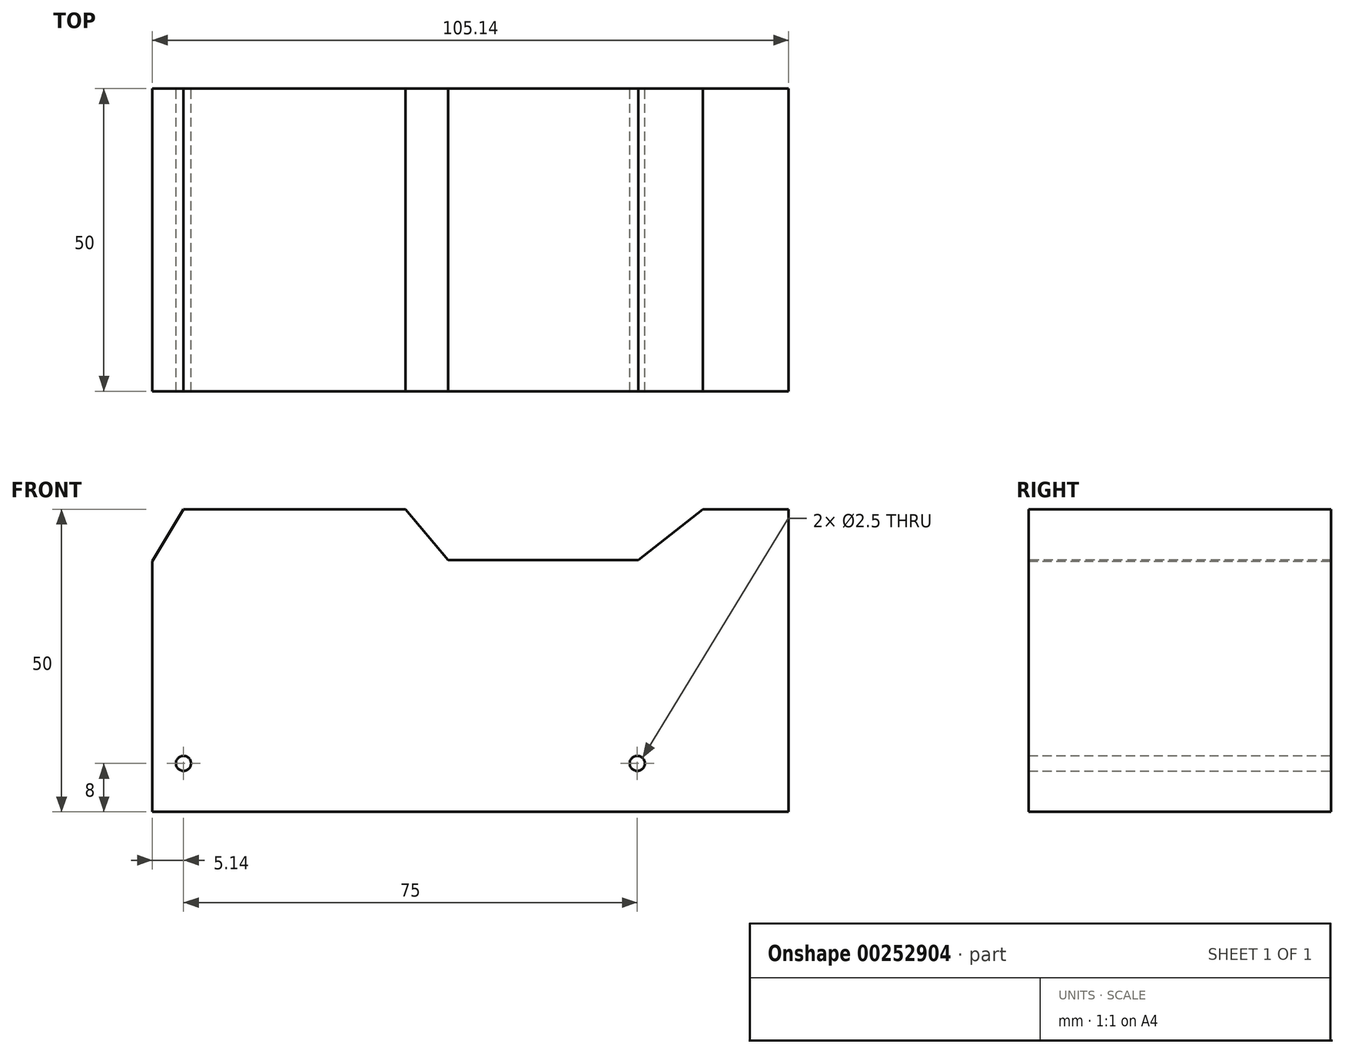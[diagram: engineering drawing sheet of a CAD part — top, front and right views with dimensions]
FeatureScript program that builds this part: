
annotation { "Feature Type Name" : "Feature", "Feature Type Description" : "" }
export const myFeature = defineFeature(function(context is Context, id is Id, definition is map)
    precondition{}
    {
        {
            var Q0;
            Q0=qCreatedBy(makeId("Front.planeOp"),FACE);
            var sketch = newSketch(context, id + "F0", { "sketchPlane" : qUnion([Q0])});
            skLineSegment(sketch, "E0.bottom", {"start": v(50, 25) * mm, "end": v(-50, 25) * mm});
            skLineSegment(sketch, "E0.top", {"start": v(50, -25) * mm, "end": v(-50, -25) * mm});
            skLineSegment(sketch, "E0.left", {"start": v(50, 25) * mm, "end": v(50, -25) * mm});
            skPoint(sketch, "E0.middle", {"position": v(0, 0) * mm});
            skLineSegment(sketch, "E1", {"start": v(-55.14, 16.43) * mm, "end": v(-50, 25) * mm});
            skLineSegment(sketch, "E2", {"start": v(50, -25) * mm, "end": v(25, -25) * mm});
            skLineSegment(sketch, "E3", {"start": v(25, -25) * mm, "end": v(25, -17) * mm});
            skLineSegment(sketch, "E4", {"start": v(-50, -18.25) * mm, "end": v(-50, -17) * mm});
            skCircle(sketch, "E5", {"center": v(-50, -17) * mm, "radius": 1.25 * mm});
            skCircle(sketch, "E6", {"center": v(25, -17) * mm, "radius": 1.25 * mm});
            skLineSegment(sketch, "E7", {"start": v(-55.14, -25) * mm, "end": v(-55.14, 16.43) * mm});
            skPoint(sketch, "E8.orphan", {"position": v(-80, -25) * mm});
            skLineSegment(sketch, "E9", {"start": v(-55.14, -25) * mm, "end": v(-50, -25) * mm});
            skSolve(sketch);
        }
        {
            var Q0;
            Q0=makeQuery(id+"F0.imprint","IMPRINT",FACE,{"disambiguationData":[TD([[makeQuery(id+"F0.imprint","IMPRINT",EDGE,{"derivedFrom":sQuery(id+"F0.wireOp",EDGE,"E0.bottom")}),1.0]])]});
            extrude(context, id + "F1", {"entities" : qUnion([Q0]), "depth" : 50 * mm});
        }
        {
            var Q0;
            Q0=makeQuery(id+"F1.opExtrude","CAP_FACE",FACE,{"disambiguationData":[OSD([sQuery(id+"F0.wireOp",EDGE,"E0.bottom"),sQuery(id+"F0.wireOp",EDGE,"E0.top"),sQuery(id+"F0.wireOp",EDGE,"E0.left"),sQuery(id+"F0.wireOp",EDGE,"AwUMNLbW-5q2J-AW1u-s40T-xbT19hCx7R6J"),sQuery(id+"F0.wireOp",EDGE,"E1"),sQuery(id+"F0.wireOp",EDGE,"E2"),sQuery(id+"F0.wireOp",EDGE,"E5"),sQuery(id+"F0.wireOp",EDGE,"E6")])],"isStart":false});
            var sketch = newSketch(context, id + "F2", { "sketchPlane" : qUnion([Q0])});
            skLineSegment(sketch, "E10", {"start": v(-6.28, 16.6) * mm, "end": v(25.16, 16.6) * mm});
            skLineSegment(sketch, "E11", {"start": v(25.16, 16.6) * mm, "end": v(44.82, 32.09) * mm});
            skLineSegment(sketch, "E12", {"start": v(44.82, 32.09) * mm, "end": v(50, 16.69) * mm});
            skPoint(sketch, "E13.start.orphan", {"position": v(-52.57, 20.72) * mm});
            skLineSegment(sketch, "E14", {"start": v(-21.47, 34.78) * mm, "end": v(-6.28, 16.6) * mm});
            skLineSegment(sketch, "E15", {"start": v(-52.57, 20.72) * mm, "end": v(-40.47, 34.18) * mm});
            skLineSegment(sketch, "E16", {"start": v(-40.47, 34.18) * mm, "end": v(-21.47, 34.78) * mm});
            skSolve(sketch);
        }
        {
            var Q0;
            Q0=makeQuery(id+"F2.imprint","IMPRINT",FACE,{"disambiguationData":[TD([[makeQuery(id+"F2.imprint","IMPRINT",EDGE,{"derivedFrom":sQuery(id+"F2.wireOp",EDGE,"E10")}),1.0]])]});
            extrude(context, id + "F3", {"entities" : qUnion([Q0]), "operationType" : NewBodyOperationType.REMOVE, "endBound" : BoundingType.THROUGH_ALL, "oppositeDirection" : true, "depth" : 25 * mm});
        }
    });
